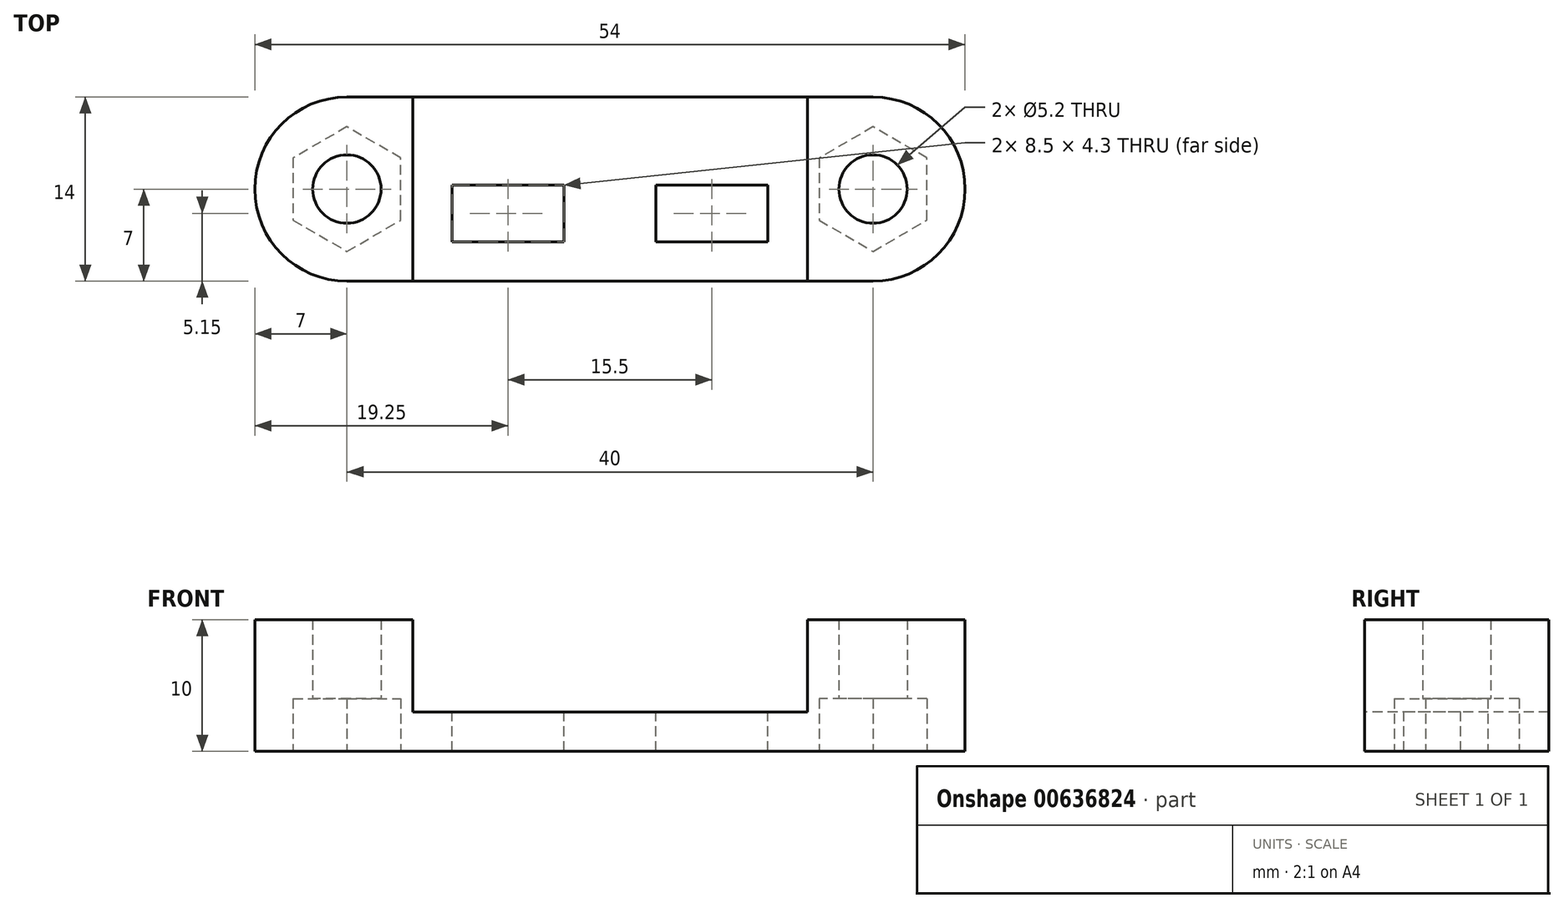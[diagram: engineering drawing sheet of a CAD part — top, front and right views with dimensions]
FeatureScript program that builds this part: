
annotation { "Feature Type Name" : "Feature", "Feature Type Description" : "" }
export const myFeature = defineFeature(function(context is Context, id is Id, definition is map)
    precondition{}
    {
        {
            var Q0;
            Q0=qCreatedBy(makeId("Top.planeOp"),FACE);
            var sketch = newSketch(context, id + "F0", { "sketchPlane" : qUnion([Q0])});
            skLineSegment(sketch, "E0.bottom", {"start": v(20, 7) * mm, "end": v(-20, 7) * mm});
            skLineSegment(sketch, "E0.top", {"start": v(20, -7) * mm, "end": v(-20, -7) * mm});
            skLineSegment(sketch, "E0.left", {"start": v(27, 0) * mm, "end": v(27, 0) * mm});
            skLineSegment(sketch, "E0.right", {"start": v(-27, 0) * mm, "end": v(-27, 0) * mm});
            skPoint(sketch, "E0.middle", {"position": v(0, 0) * mm});
            skPoint(sketch, "E1.visualSharp", {"position": v(-27, 7) * mm});
            skArc(sketch, "E1.filletArc", {"start": v(-20, 7) * mm, "mid": v(-24.95, 4.95) * mm, "end": v(-27, 0) * mm});
            skPoint(sketch, "E2.visualSharp", {"position": v(-27, -7) * mm});
            skArc(sketch, "E2.filletArc", {"start": v(-27, 0) * mm, "mid": v(-24.95, -4.95) * mm, "end": v(-20, -7) * mm});
            skPoint(sketch, "E3.visualSharp", {"position": v(27, -7) * mm});
            skArc(sketch, "E3.filletArc", {"start": v(20, -7) * mm, "mid": v(24.95, -4.95) * mm, "end": v(27, 0) * mm});
            skPoint(sketch, "E4.visualSharp", {"position": v(27, 7) * mm});
            skArc(sketch, "E4.filletArc", {"start": v(27, 0) * mm, "mid": v(24.95, 4.95) * mm, "end": v(20, 7) * mm});
            skCircle(sketch, "E5", {"center": v(-20, 0) * mm, "radius": 2.6 * mm});
            skCircle(sketch, "E6", {"center": v(20, 0) * mm, "radius": 2.6 * mm});
            skSolve(sketch);
        }
        {
            var Q0;
            Q0=makeQuery(id+"F0.imprint","IMPRINT",FACE,{"disambiguationData":[TD([[makeQuery(id+"F0.imprint","IMPRINT",EDGE,{"derivedFrom":sQuery(id+"F0.wireOp",EDGE,"E0.bottom")}),1.0]])]});
            extrude(context, id + "F1", {"entities" : qUnion([Q0]), "depth" : 10 * mm, "offsetDistance" : 25 * mm});
        }
        {
            var Q0;
            Q0=makeQuery(id+"F1.opExtrude","CAP_FACE",FACE,{"disambiguationData":[OSD([sQuery(id+"F0.wireOp",EDGE,"E0.bottom"),sQuery(id+"F0.wireOp",EDGE,"E0.top"),sQuery(id+"F0.wireOp",EDGE,"E1.filletArc"),sQuery(id+"F0.wireOp",EDGE,"E2.filletArc"),sQuery(id+"F0.wireOp",EDGE,"E3.filletArc"),sQuery(id+"F0.wireOp",EDGE,"E4.filletArc"),sQuery(id+"F0.wireOp",EDGE,"E5"),sQuery(id+"F0.wireOp",EDGE,"E6")])],"isStart":false});
            var sketch = newSketch(context, id + "F2", { "sketchPlane" : qUnion([Q0])});
            skLineSegment(sketch, "E7.bottom", {"start": v(-15, 7) * mm, "end": v(15, 7) * mm});
            skLineSegment(sketch, "E7.top", {"start": v(-15, -7) * mm, "end": v(15, -7) * mm});
            skLineSegment(sketch, "E7.left", {"start": v(-15, 7) * mm, "end": v(-15, -7) * mm});
            skLineSegment(sketch, "E7.right", {"start": v(15, 7) * mm, "end": v(15, -7) * mm});
            skPoint(sketch, "E7.middle", {"position": v(0, 0) * mm});
            skSolve(sketch);
        }
        {
            var Q0;
            Q0 = qSketchRegion(id + "F2", true);
            extrude(context, id + "F3", {"entities" : qUnion([Q0]), "operationType" : NewBodyOperationType.REMOVE, "oppositeDirection" : true, "depth" : 7 * mm, "offsetDistance" : 25 * mm});
        }
        {
            var Q0;
            Q0=makeQuery(id+"F3.boolean.opBoolean","COPY",FACE,{"derivedFrom":makeQuery(id+"F3.opExtrude","CAP_FACE",FACE,{"disambiguationData":[OSD([sQuery(id+"F2.wireOp",EDGE,"E7.bottom"),sQuery(id+"F2.wireOp",EDGE,"E7.top"),sQuery(id+"F2.wireOp",EDGE,"E7.left"),sQuery(id+"F2.wireOp",EDGE,"E7.right")])],"isStart":false})});
            var sketch = newSketch(context, id + "F4", { "sketchPlane" : qUnion([Q0])});
            skLineSegment(sketch, "E8.bottom", {"start": v(-3.5, 0.3) * mm, "end": v(-12, 0.3) * mm});
            skLineSegment(sketch, "E8.top", {"start": v(-3.5, -4) * mm, "end": v(-12, -4) * mm});
            skLineSegment(sketch, "E8.left", {"start": v(-3.5, 0.3) * mm, "end": v(-3.5, -4) * mm});
            skLineSegment(sketch, "E8.right", {"start": v(-12, 0.3) * mm, "end": v(-12, -4) * mm});
            skPoint(sketch, "E9.1.0.0", {"position": v(7.75, 0) * mm});
            skLineSegment(sketch, "E9.1.0.1", {"start": v(12, 0.3) * mm, "end": v(3.5, 0.3) * mm});
            skLineSegment(sketch, "E9.1.0.2", {"start": v(12, -4) * mm, "end": v(3.5, -4) * mm});
            skLineSegment(sketch, "E9.1.0.3", {"start": v(12, 0.3) * mm, "end": v(12, -4) * mm});
            skLineSegment(sketch, "E9.1.0.4", {"start": v(3.5, 0.3) * mm, "end": v(3.5, -4) * mm});
            skLineSegment(sketch, "E9.direction1", {"start": v(-12, -4) * mm, "end": v(3.5, -4) * mm, "construction": true});
            skSolve(sketch);
        }
        {
            var Q0;
            Q0 = qSketchRegion(id + "F4", true);
            extrude(context, id + "F5", {"entities" : qUnion([Q0]), "operationType" : NewBodyOperationType.REMOVE, "oppositeDirection" : true, "depth" : 25 * mm, "offsetDistance" : 25 * mm});
        }
        {
            var Q0;
            Q0=makeQuery(id+"F1.opExtrude","CAP_FACE",FACE,{"disambiguationData":[OSD([sQuery(id+"F0.wireOp",EDGE,"E0.bottom"),sQuery(id+"F0.wireOp",EDGE,"E0.top"),sQuery(id+"F0.wireOp",EDGE,"E1.filletArc"),sQuery(id+"F0.wireOp",EDGE,"E2.filletArc"),sQuery(id+"F0.wireOp",EDGE,"E3.filletArc"),sQuery(id+"F0.wireOp",EDGE,"E4.filletArc"),sQuery(id+"F0.wireOp",EDGE,"E5"),sQuery(id+"F0.wireOp",EDGE,"E6")])],"isStart":true});
            var sketch = newSketch(context, id + "F6", { "sketchPlane" : qUnion([Q0])});
            skCircle(sketch, "E10.cCircle", {"center": v(-20, 0) * mm, "radius": 4.1 * mm, "construction": true});
            skLineSegment(sketch, "E10.0", {"start": v(-15.9, 2.37) * mm, "end": v(-15.9, -2.37) * mm});
            skLineSegment(sketch, "E10.1", {"start": v(-15.9, -2.37) * mm, "end": v(-20, -4.73) * mm});
            skLineSegment(sketch, "E10.2", {"start": v(-20, -4.73) * mm, "end": v(-24.1, -2.37) * mm});
            skLineSegment(sketch, "E10.3", {"start": v(-24.1, -2.37) * mm, "end": v(-24.1, 2.37) * mm});
            skLineSegment(sketch, "E10.4", {"start": v(-24.1, 2.37) * mm, "end": v(-20, 4.73) * mm});
            skLineSegment(sketch, "E10.5", {"start": v(-20, 4.73) * mm, "end": v(-15.9, 2.37) * mm});
            skPoint(sketch, "E10.0.midPoint", {"position": v(-15.9, 0) * mm});
            skCircle(sketch, "E11.cCircle", {"center": v(20, 0) * mm, "radius": 4.1 * mm, "construction": true});
            skLineSegment(sketch, "E11.0", {"start": v(15.9, -2.37) * mm, "end": v(15.9, 2.37) * mm});
            skLineSegment(sketch, "E11.1", {"start": v(15.9, 2.37) * mm, "end": v(20, 4.73) * mm});
            skLineSegment(sketch, "E11.2", {"start": v(20, 4.73) * mm, "end": v(24.1, 2.37) * mm});
            skLineSegment(sketch, "E11.3", {"start": v(24.1, 2.37) * mm, "end": v(24.1, -2.37) * mm});
            skLineSegment(sketch, "E11.4", {"start": v(24.1, -2.37) * mm, "end": v(20, -4.73) * mm});
            skLineSegment(sketch, "E11.5", {"start": v(20, -4.73) * mm, "end": v(15.9, -2.37) * mm});
            skPoint(sketch, "E11.0.midPoint", {"position": v(15.9, 0) * mm});
            skSolve(sketch);
        }
        {
            var Q0;
            Q0=makeQuery(id+"F6.imprint","IMPRINT",FACE,{"disambiguationData":[TD([[makeQuery(id+"F6.imprint","IMPRINT",EDGE,{"derivedFrom":sQuery(id+"F6.wireOp",EDGE,"E10.0")}),-1.0]])]});
            var Q1;
            Q1=makeQuery(id+"F6.imprint","IMPRINT",FACE,{"disambiguationData":[TD([[makeQuery(id+"F6.imprint","IMPRINT",EDGE,{"derivedFrom":sQuery(id+"F6.wireOp",EDGE,"E11.0")}),-1.0]])]});
            extrude(context, id + "F7", {"entities" : qUnion([Q0, Q1]), "operationType" : NewBodyOperationType.REMOVE, "oppositeDirection" : true, "depth" : 4 * mm, "offsetDistance" : 25 * mm});
        }
    });
